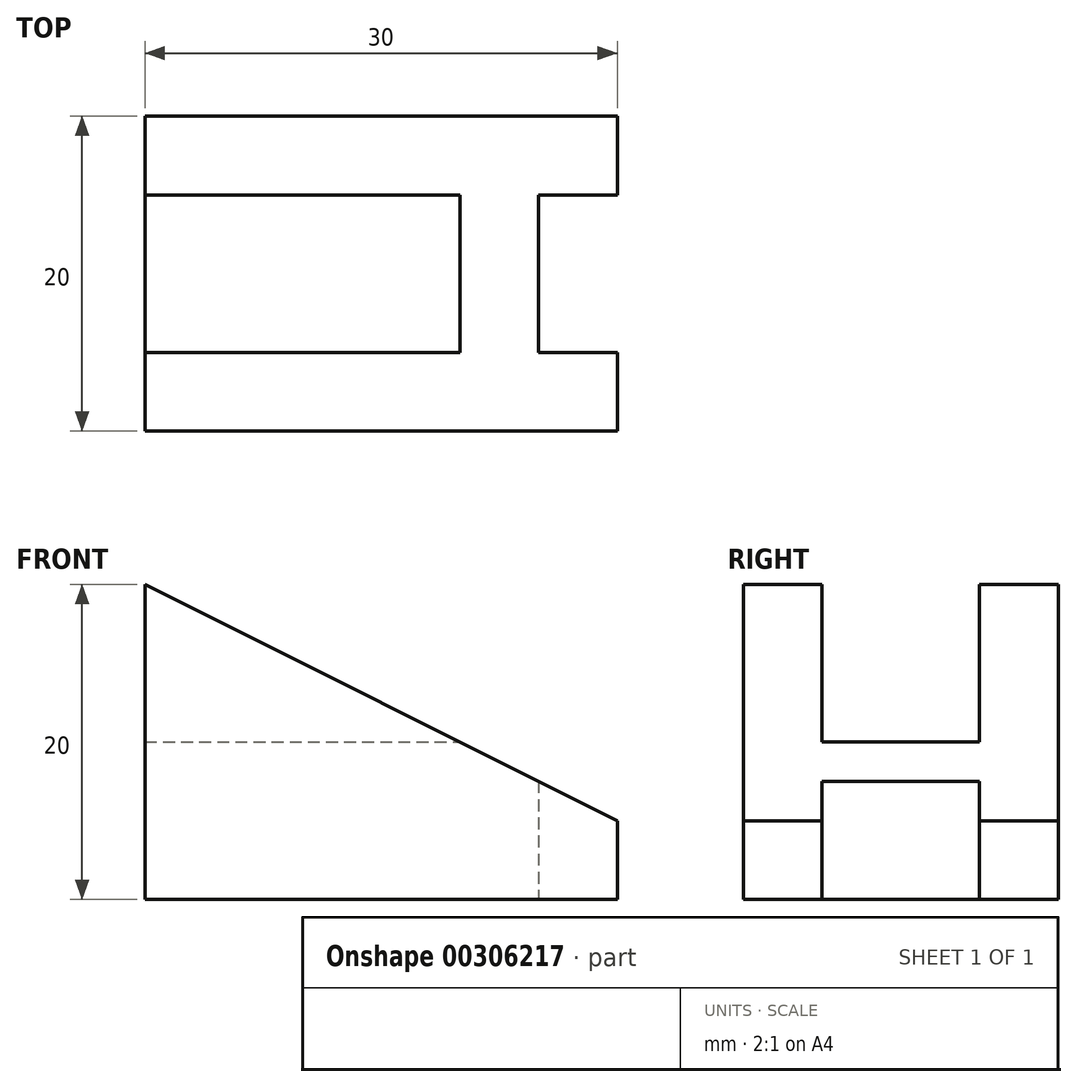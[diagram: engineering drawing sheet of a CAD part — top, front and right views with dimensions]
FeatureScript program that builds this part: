
annotation { "Feature Type Name" : "Feature", "Feature Type Description" : "" }
export const myFeature = defineFeature(function(context is Context, id is Id, definition is map)
    precondition{}
    {
        {
            var Q0;
            Q0=qCreatedBy(makeId("Front.planeOp"),FACE);
            var sketch = newSketch(context, id + "F0", { "sketchPlane" : qUnion([Q0])});
            skLineSegment(sketch, "E0", {"start": v(0, 20) * mm, "end": v(0, 0) * mm});
            skLineSegment(sketch, "E1", {"start": v(0, 0) * mm, "end": v(30, 0) * mm});
            skLineSegment(sketch, "E2", {"start": v(30, 0) * mm, "end": v(30, 5) * mm});
            skLineSegment(sketch, "E3", {"start": v(30, 5) * mm, "end": v(0, 20) * mm});
            skLineSegment(sketch, "E4", {"start": v(0, 10) * mm, "end": v(20, 10) * mm});
            skLineSegment(sketch, "E5", {"start": v(25, 7.5) * mm, "end": v(25, 0) * mm});
            skSolve(sketch);
        }
        {
            var Q0;
            Q0 = qSketchRegion(id + "F0", true);
            extrude(context, id + "F1", {"entities" : qUnion([Q0]), "endBound" : BoundingType.SYMMETRIC, "depth" : 20 * mm});
        }
        {
            var Q0;
            {var subQ3=sQuery(id+"F0.wireOp",EDGE,"E4");Q0=makeQuery(id+"F0.imprint","IMPRINT",FACE,{"disambiguationData":[TD([[makeQuery(id+"F0.imprint","IMPRINT",EDGE,{"derivedFrom":subQ3}),1.0]])]});}
            var Q1;
            {var subQ0=sQuery(id+"F0.wireOp",EDGE,"E2");Q1=makeQuery(id+"F0.imprint","IMPRINT",FACE,{"disambiguationData":[TD([[makeQuery(id+"F0.imprint","IMPRINT",EDGE,{"derivedFrom":subQ0}),1.0]])]});}
            extrude(context, id + "F2", {"entities" : qUnion([Q0, Q1]), "operationType" : NewBodyOperationType.REMOVE, "endBound" : BoundingType.SYMMETRIC, "oppositeDirection" : true, "depth" : 10 * mm});
        }
    });
